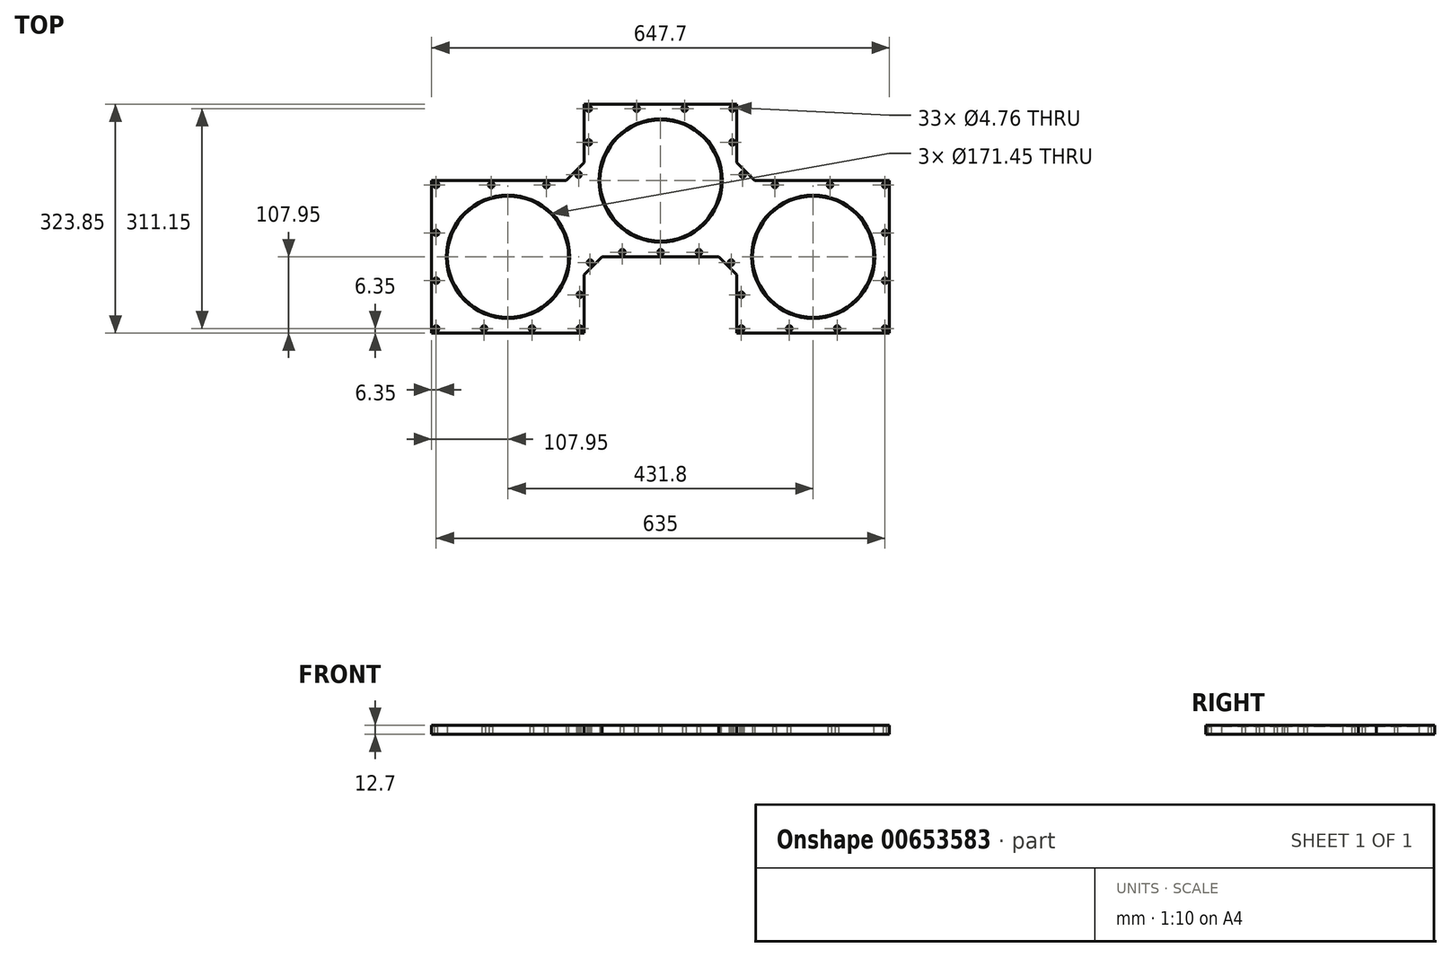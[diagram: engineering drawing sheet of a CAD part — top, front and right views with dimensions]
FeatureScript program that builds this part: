
annotation { "Feature Type Name" : "Feature", "Feature Type Description" : "" }
export const myFeature = defineFeature(function(context is Context, id is Id, definition is map)
    precondition{}
    {
        {
            var Q0;
            Q0=qCreatedBy(makeId("Top.planeOp"),FACE);
            var sketch = newSketch(context, id + "F0", { "sketchPlane" : qUnion([Q0])});
            skCircle(sketch, "E0", {"center": v(0, 107.95) * mm, "radius": 85.73 * mm});
            skCircle(sketch, "E1", {"center": v(-215.9, 0) * mm, "radius": 85.73 * mm});
            skCircle(sketch, "E2", {"center": v(215.9, 0) * mm, "radius": 85.73 * mm});
            skLineSegment(sketch, "E3.bottom", {"start": v(-133.35, 107.95) * mm, "end": v(-323.85, 107.95) * mm});
            skLineSegment(sketch, "E3.top", {"start": v(-107.95, -107.95) * mm, "end": v(-323.85, -107.95) * mm});
            skLineSegment(sketch, "E3.right", {"start": v(-323.85, 107.95) * mm, "end": v(-323.85, -107.95) * mm});
            skLineSegment(sketch, "E4.bottom", {"start": v(-82.55, 0) * mm, "end": v(82.55, 0) * mm});
            skLineSegment(sketch, "E4.top", {"start": v(-107.95, 215.9) * mm, "end": v(107.95, 215.9) * mm});
            skLineSegment(sketch, "E4.left", {"start": v(-107.95, 133.35) * mm, "end": v(-107.95, 215.9) * mm});
            skLineSegment(sketch, "E5.bottom", {"start": v(323.85, 107.95) * mm, "end": v(133.35, 107.95) * mm});
            skLineSegment(sketch, "E5.top", {"start": v(323.85, -107.95) * mm, "end": v(107.95, -107.95) * mm});
            skLineSegment(sketch, "E5.left", {"start": v(323.85, 107.95) * mm, "end": v(323.85, -107.95) * mm});
            skLineSegment(sketch, "E5.right", {"start": v(107.95, -25.4) * mm, "end": v(107.95, -107.95) * mm});
            skLineSegment(sketch, "E6", {"start": v(107.95, 133.35) * mm, "end": v(133.35, 107.95) * mm});
            skLineSegment(sketch, "E7", {"start": v(82.55, 0) * mm, "end": v(107.95, -25.4) * mm});
            skLineSegment(sketch, "E8", {"start": v(-82.55, 0) * mm, "end": v(-107.95, -25.4) * mm});
            skLineSegment(sketch, "E9", {"start": v(-107.95, 133.35) * mm, "end": v(-133.35, 107.95) * mm});
            skLineSegment(sketch, "E10.trimOffspring", {"start": v(107.95, 133.35) * mm, "end": v(107.95, 215.9) * mm});
            skPoint(sketch, "E11.orphan", {"position": v(107.95, 0) * mm});
            skPoint(sketch, "E12.orphan", {"position": v(107.95, 107.95) * mm});
            skLineSegment(sketch, "E13.trimOffspring", {"start": v(-107.95, -25.4) * mm, "end": v(-107.95, -107.95) * mm});
            skPoint(sketch, "E3.left.end.orphan", {"position": v(-107.95, 0) * mm});
            skPoint(sketch, "E14.orphan", {"position": v(-107.95, 107.95) * mm});
            skLineSegment(sketch, "E15", {"start": v(-107.95, 133.35) * mm, "end": v(-107.95, -25.4) * mm, "construction": true});
            skLineSegment(sketch, "E16", {"start": v(-107.95, 0) * mm, "end": v(-82.55, 0) * mm, "construction": true});
            skLineSegment(sketch, "E17", {"start": v(-107.95, 107.95) * mm, "end": v(-133.35, 107.95) * mm, "construction": true});
            skLineSegment(sketch, "E18", {"start": v(107.95, 133.35) * mm, "end": v(107.95, -25.4) * mm, "construction": true});
            skLineSegment(sketch, "E19", {"start": v(107.95, 0) * mm, "end": v(82.55, 0) * mm, "construction": true});
            skLineSegment(sketch, "E20", {"start": v(107.95, 107.95) * mm, "end": v(133.35, 107.95) * mm, "construction": true});
            skLineSegment(sketch, "E21", {"start": v(0, 0) * mm, "end": v(0, 215.9) * mm, "construction": true});
            skSolve(sketch);
        }
        {
            var Q0;
            Q0=makeQuery(id+"F0.imprint","IMPRINT",FACE,{"disambiguationData":[TD([[makeQuery(id+"F0.imprint","IMPRINT",EDGE,{"derivedFrom":sQuery(id+"F0.wireOp",EDGE,"9jGv9sEQ-ModP-p4JU-NunE-Bp6go0j5906w.bottom")}),-1.0]])]});
            var Q1;
            Q1=makeQuery(id+"F0.imprint","IMPRINT",FACE,{"disambiguationData":[TD([[makeQuery(id+"F0.imprint","IMPRINT",EDGE,{"derivedFrom":sQuery(id+"F0.wireOp",EDGE,"E0")}),-1.0]])]});
            extrude(context, id + "F1", {"entities" : qUnion([Q0, Q1]), "depth" : 12.7 * mm, "offsetDistance" : 25.4 * mm});
        }
        {
            var Q0;
            Q0=makeQuery(id+"F1.opExtrude","CAP_FACE",FACE,{"disambiguationData":[OSD([sQuery(id+"F0.wireOp",EDGE,"E0"),sQuery(id+"F0.wireOp",EDGE,"E1"),sQuery(id+"F0.wireOp",EDGE,"E2"),sQuery(id+"F0.wireOp",EDGE,"E3.bottom"),sQuery(id+"F0.wireOp",EDGE,"E3.top"),sQuery(id+"F0.wireOp",EDGE,"E3.right"),sQuery(id+"F0.wireOp",EDGE,"E4.bottom"),sQuery(id+"F0.wireOp",EDGE,"E4.top"),sQuery(id+"F0.wireOp",EDGE,"E4.left"),sQuery(id+"F0.wireOp",EDGE,"E5.bottom"),sQuery(id+"F0.wireOp",EDGE,"E5.top"),sQuery(id+"F0.wireOp",EDGE,"E5.left"),sQuery(id+"F0.wireOp",EDGE,"E5.right"),sQuery(id+"F0.wireOp",EDGE,"E6"),sQuery(id+"F0.wireOp",EDGE,"E7"),sQuery(id+"F0.wireOp",EDGE,"E8"),sQuery(id+"F0.wireOp",EDGE,"E9"),sQuery(id+"F0.wireOp",EDGE,"E10.trimOffspring"),sQuery(id+"F0.wireOp",EDGE,"E13.trimOffspring")])],"isStart":false});
            var sketch = newSketch(context, id + "F2", { "sketchPlane" : qUnion([Q0])});
            skLineSegment(sketch, "E22.0", {"start": v(317.5, 101.6) * mm, "end": v(130.72, 101.6) * mm});
            skLineSegment(sketch, "E22.1", {"start": v(317.5, -101.6) * mm, "end": v(317.5, 101.6) * mm});
            skLineSegment(sketch, "E22.2", {"start": v(114.3, -101.6) * mm, "end": v(317.5, -101.6) * mm});
            skLineSegment(sketch, "E22.3", {"start": v(114.3, -22.77) * mm, "end": v(114.3, -101.6) * mm});
            skLineSegment(sketch, "E22.4", {"start": v(85.18, 6.35) * mm, "end": v(114.3, -22.77) * mm});
            skLineSegment(sketch, "E22.5", {"start": v(-101.6, 130.72) * mm, "end": v(-130.72, 101.6) * mm});
            skLineSegment(sketch, "E22.6", {"start": v(-101.6, 209.55) * mm, "end": v(-101.6, 130.72) * mm});
            skLineSegment(sketch, "E22.7", {"start": v(101.6, 209.55) * mm, "end": v(-101.6, 209.55) * mm});
            skLineSegment(sketch, "E22.8", {"start": v(101.6, 130.72) * mm, "end": v(101.6, 209.55) * mm});
            skLineSegment(sketch, "E22.9", {"start": v(-130.72, 101.6) * mm, "end": v(-317.5, 101.6) * mm});
            skLineSegment(sketch, "E22.10", {"start": v(-317.5, 101.6) * mm, "end": v(-317.5, -101.6) * mm});
            skLineSegment(sketch, "E22.11", {"start": v(-317.5, -101.6) * mm, "end": v(-114.3, -101.6) * mm});
            skLineSegment(sketch, "E22.12", {"start": v(-114.3, -101.6) * mm, "end": v(-114.3, -22.77) * mm});
            skLineSegment(sketch, "E22.13", {"start": v(-114.3, -22.77) * mm, "end": v(-85.18, 6.35) * mm});
            skLineSegment(sketch, "E22.14", {"start": v(130.72, 101.6) * mm, "end": v(101.6, 130.72) * mm});
            skLineSegment(sketch, "E22.15", {"start": v(-85.18, 6.35) * mm, "end": v(85.18, 6.35) * mm});
            skPoint(sketch, "E23", {"position": v(-33.87, 209.55) * mm});
            skPoint(sketch, "E24", {"position": v(33.87, 209.55) * mm});
            skPoint(sketch, "E25", {"position": v(116.16, 116.16) * mm});
            skPoint(sketch, "E26", {"position": v(-116.16, 116.16) * mm});
            skPoint(sketch, "E27", {"position": v(-161.72, 101.6) * mm});
            skPoint(sketch, "E28", {"position": v(-239.6, 101.6) * mm});
            skPoint(sketch, "E29", {"position": v(-317.5, 33.87) * mm});
            skPoint(sketch, "E30", {"position": v(-317.5, -33.87) * mm});
            skPoint(sketch, "E31", {"position": v(-249.77, -101.6) * mm});
            skPoint(sketch, "E32", {"position": v(-182.03, -101.6) * mm});
            skPoint(sketch, "E33", {"position": v(-114.3, -53.77) * mm});
            skPoint(sketch, "E34", {"position": v(-99.74, -8.2) * mm});
            skPoint(sketch, "E35", {"position": v(-54.18, 6.35) * mm});
            skPoint(sketch, "E36", {"position": v(54.18, 6.35) * mm});
            skPoint(sketch, "E37", {"position": v(99.74, -8.2) * mm});
            skPoint(sketch, "E38", {"position": v(114.3, -53.77) * mm});
            skPoint(sketch, "E39", {"position": v(182.03, -101.6) * mm});
            skPoint(sketch, "E40", {"position": v(249.77, -101.6) * mm});
            skPoint(sketch, "E41", {"position": v(317.5, -33.87) * mm});
            skPoint(sketch, "E42", {"position": v(317.5, 33.87) * mm});
            skPoint(sketch, "E43", {"position": v(239.6, 101.6) * mm});
            skPoint(sketch, "E44", {"position": v(161.72, 101.6) * mm});
            skPoint(sketch, "E45", {"position": v(101.6, 161.72) * mm});
            skPoint(sketch, "E46", {"position": v(-101.6, 161.72) * mm});
            skLineSegment(sketch, "E47", {"start": v(-101.6, 161.72) * mm, "end": v(-116.16, 116.16) * mm, "construction": true});
            skLineSegment(sketch, "E48", {"start": v(-116.16, 116.16) * mm, "end": v(-161.72, 101.6) * mm, "construction": true});
            skLineSegment(sketch, "E49", {"start": v(-99.74, -8.2) * mm, "end": v(-54.18, 6.35) * mm, "construction": true});
            skLineSegment(sketch, "E50", {"start": v(-99.74, -8.2) * mm, "end": v(-114.3, -53.77) * mm, "construction": true});
            skLineSegment(sketch, "E51", {"start": v(99.74, -8.2) * mm, "end": v(54.18, 6.35) * mm, "construction": true});
            skLineSegment(sketch, "E52", {"start": v(99.74, -8.2) * mm, "end": v(114.3, -53.77) * mm, "construction": true});
            skLineSegment(sketch, "E53", {"start": v(116.16, 116.16) * mm, "end": v(161.72, 101.6) * mm, "construction": true});
            skLineSegment(sketch, "E54", {"start": v(116.16, 116.16) * mm, "end": v(101.6, 161.72) * mm, "construction": true});
            skLineSegment(sketch, "E55", {"start": v(-101.6, 161.72) * mm, "end": v(-101.6, 209.55) * mm, "construction": true});
            skLineSegment(sketch, "E56", {"start": v(-101.6, 209.55) * mm, "end": v(-33.87, 209.55) * mm, "construction": true});
            skLineSegment(sketch, "E57", {"start": v(-33.87, 209.55) * mm, "end": v(33.87, 209.55) * mm, "construction": true});
            skLineSegment(sketch, "E58", {"start": v(33.87, 209.55) * mm, "end": v(101.6, 209.55) * mm, "construction": true});
            skLineSegment(sketch, "E59", {"start": v(-161.72, 101.6) * mm, "end": v(-239.6, 101.6) * mm, "construction": true});
            skLineSegment(sketch, "E60", {"start": v(-239.6, 101.6) * mm, "end": v(-317.5, 101.6) * mm, "construction": true});
            skLineSegment(sketch, "E61", {"start": v(-317.5, 101.6) * mm, "end": v(-317.5, 33.87) * mm, "construction": true});
            skLineSegment(sketch, "E62", {"start": v(-317.5, 33.87) * mm, "end": v(-317.5, -33.87) * mm, "construction": true});
            skLineSegment(sketch, "E63", {"start": v(-317.5, -33.87) * mm, "end": v(-317.5, -101.6) * mm, "construction": true});
            skLineSegment(sketch, "E64", {"start": v(-317.5, -101.6) * mm, "end": v(-249.77, -101.6) * mm, "construction": true});
            skLineSegment(sketch, "E65", {"start": v(-249.77, -101.6) * mm, "end": v(-182.03, -101.6) * mm, "construction": true});
            skLineSegment(sketch, "E66", {"start": v(-182.03, -101.6) * mm, "end": v(-114.3, -101.6) * mm, "construction": true});
            skPoint(sketch, "E67", {"position": v(0, 6.35) * mm});
            skLineSegment(sketch, "E68", {"start": v(161.72, 101.6) * mm, "end": v(239.6, 101.6) * mm, "construction": true});
            skLineSegment(sketch, "E69", {"start": v(239.6, 101.6) * mm, "end": v(317.5, 101.6) * mm, "construction": true});
            skLineSegment(sketch, "E70", {"start": v(317.5, 101.6) * mm, "end": v(317.5, 33.87) * mm, "construction": true});
            skLineSegment(sketch, "E71", {"start": v(317.5, 33.87) * mm, "end": v(317.5, -33.87) * mm, "construction": true});
            skLineSegment(sketch, "E72", {"start": v(317.5, -33.87) * mm, "end": v(317.5, -101.6) * mm, "construction": true});
            skLineSegment(sketch, "E73", {"start": v(317.5, -101.6) * mm, "end": v(249.77, -101.6) * mm, "construction": true});
            skLineSegment(sketch, "E74", {"start": v(249.77, -101.6) * mm, "end": v(182.03, -101.6) * mm, "construction": true});
            skLineSegment(sketch, "E75", {"start": v(182.03, -101.6) * mm, "end": v(114.3, -101.6) * mm, "construction": true});
            skSolve(sketch);
        }
        {
            var Q0;
            Q0=sQuery(id+"F2.wireOp",VERTEX,"E28");
            var Q1;
            Q1=sQuery(id+"F2.wireOp",VERTEX,"E27");
            var Q2;
            Q2=sQuery(id+"F2.wireOp",VERTEX,"E26");
            var Q3;
            Q3=sQuery(id+"F2.wireOp",VERTEX,"E46");
            var Q4;
            Q4=sQuery(id+"F2.wireOp",VERTEX,"E22.6.start");
            var Q5;
            Q5=sQuery(id+"F2.wireOp",VERTEX,"E23");
            var Q6;
            Q6=sQuery(id+"F2.wireOp",VERTEX,"E24");
            var Q7;
            Q7=sQuery(id+"F2.wireOp",VERTEX,"E22.7.start");
            var Q8;
            Q8=sQuery(id+"F2.wireOp",VERTEX,"E45");
            var Q9;
            Q9=sQuery(id+"F2.wireOp",VERTEX,"E25");
            var Q10;
            Q10=sQuery(id+"F2.wireOp",VERTEX,"E44");
            var Q11;
            Q11=sQuery(id+"F2.wireOp",VERTEX,"E43");
            var Q12;
            Q12=sQuery(id+"F2.wireOp",VERTEX,"E42");
            var Q13;
            Q13=sQuery(id+"F2.wireOp",VERTEX,"E22.0.start");
            var Q14;
            Q14=sQuery(id+"F2.wireOp",VERTEX,"E41");
            var Q15;
            Q15=sQuery(id+"F2.wireOp",VERTEX,"E22.2.end");
            var Q16;
            Q16=sQuery(id+"F2.wireOp",VERTEX,"E40");
            var Q17;
            Q17=sQuery(id+"F2.wireOp",VERTEX,"E39");
            var Q18;
            Q18=sQuery(id+"F2.wireOp",VERTEX,"E38");
            var Q19;
            Q19=sQuery(id+"F2.wireOp",VERTEX,"E22.3.end");
            var Q20;
            Q20=sQuery(id+"F2.wireOp",VERTEX,"E37");
            var Q21;
            Q21=sQuery(id+"F2.wireOp",VERTEX,"E36");
            var Q22;
            Q22=sQuery(id+"F2.wireOp",VERTEX,"E67");
            var Q23;
            Q23=sQuery(id+"F2.wireOp",VERTEX,"E35");
            var Q24;
            Q24=sQuery(id+"F2.wireOp",VERTEX,"E34");
            var Q25;
            Q25=sQuery(id+"F2.wireOp",VERTEX,"E33");
            var Q26;
            Q26=sQuery(id+"F2.wireOp",VERTEX,"E22.12.start");
            var Q27;
            Q27=sQuery(id+"F2.wireOp",VERTEX,"E32");
            var Q28;
            Q28=sQuery(id+"F2.wireOp",VERTEX,"E31");
            var Q29;
            Q29=sQuery(id+"F2.wireOp",VERTEX,"E64.start");
            var Q30;
            Q30=sQuery(id+"F2.wireOp",VERTEX,"E30");
            var Q31;
            Q31=sQuery(id+"F2.wireOp",VERTEX,"E29");
            var Q32;
            Q32=sQuery(id+"F2.wireOp",VERTEX,"E22.10.start");
            var Q33;
            Q33=makeQuery(id+"F1.opExtrude","SWEPT_BODY",BODY,{"disambiguationData":[OSD([sQuery(id+"F0.wireOp",EDGE,"E0"),sQuery(id+"F0.wireOp",EDGE,"E1"),sQuery(id+"F0.wireOp",EDGE,"E2"),sQuery(id+"F0.wireOp",EDGE,"E3.bottom"),sQuery(id+"F0.wireOp",EDGE,"E3.top"),sQuery(id+"F0.wireOp",EDGE,"E3.right"),sQuery(id+"F0.wireOp",EDGE,"E4.bottom"),sQuery(id+"F0.wireOp",EDGE,"E4.top"),sQuery(id+"F0.wireOp",EDGE,"E4.left"),sQuery(id+"F0.wireOp",EDGE,"E5.bottom"),sQuery(id+"F0.wireOp",EDGE,"E5.top"),sQuery(id+"F0.wireOp",EDGE,"E5.left"),sQuery(id+"F0.wireOp",EDGE,"E5.right"),sQuery(id+"F0.wireOp",EDGE,"E6"),sQuery(id+"F0.wireOp",EDGE,"E7"),sQuery(id+"F0.wireOp",EDGE,"E8"),sQuery(id+"F0.wireOp",EDGE,"E9"),sQuery(id+"F0.wireOp",EDGE,"E10.trimOffspring"),sQuery(id+"F0.wireOp",EDGE,"E13.trimOffspring")])]});
            hole(context, id + "F3", {"style" : HoleStyle.C_SINK, "endStyle" : HoleEndStyle.THROUGH, "holeDiameter" : 4.76 * mm, "cSinkDiameter" : 7.94 * mm, "cSinkAngle" : 85 * degree, "majorDiameter" : 6.35 * mm, "isTappedThrough" : true, "tappedDepth" : 12.7 * mm, "tapClearance" : 3, "locations" : qUnion([Q0, Q1, Q2, Q3, Q4, Q5, Q6, Q7, Q8, Q9, Q10, Q11, Q12, Q13, Q14, Q15, Q16, Q17, Q18, Q19, Q20, Q21, Q22, Q23, Q24, Q25, Q26, Q27, Q28, Q29, Q30, Q31, Q32]), "scope" : qUnion([Q33])});
        }
        {
            var Q0;
            Q0=makeQuery(id+"F1.opExtrude","CAP_EDGE",EDGE,{"disambiguationData":[OSD([sQuery(id+"F0.wireOp",EDGE,"E0")])],"isStart":false});
            var Q1;
            Q1=makeQuery(id+"F1.opExtrude","CAP_EDGE",EDGE,{"disambiguationData":[OSD([sQuery(id+"F0.wireOp",EDGE,"E1")])],"isStart":false});
            var Q2;
            Q2=makeQuery(id+"F1.opExtrude","CAP_EDGE",EDGE,{"disambiguationData":[OSD([sQuery(id+"F0.wireOp",EDGE,"E2")])],"isStart":false});
            chamfer(context, id + "F4", {"entities" : qUnion([Q0, Q1, Q2]), "width" : 1.59 * mm, "tangentPropagation" : true});
        }
    });
